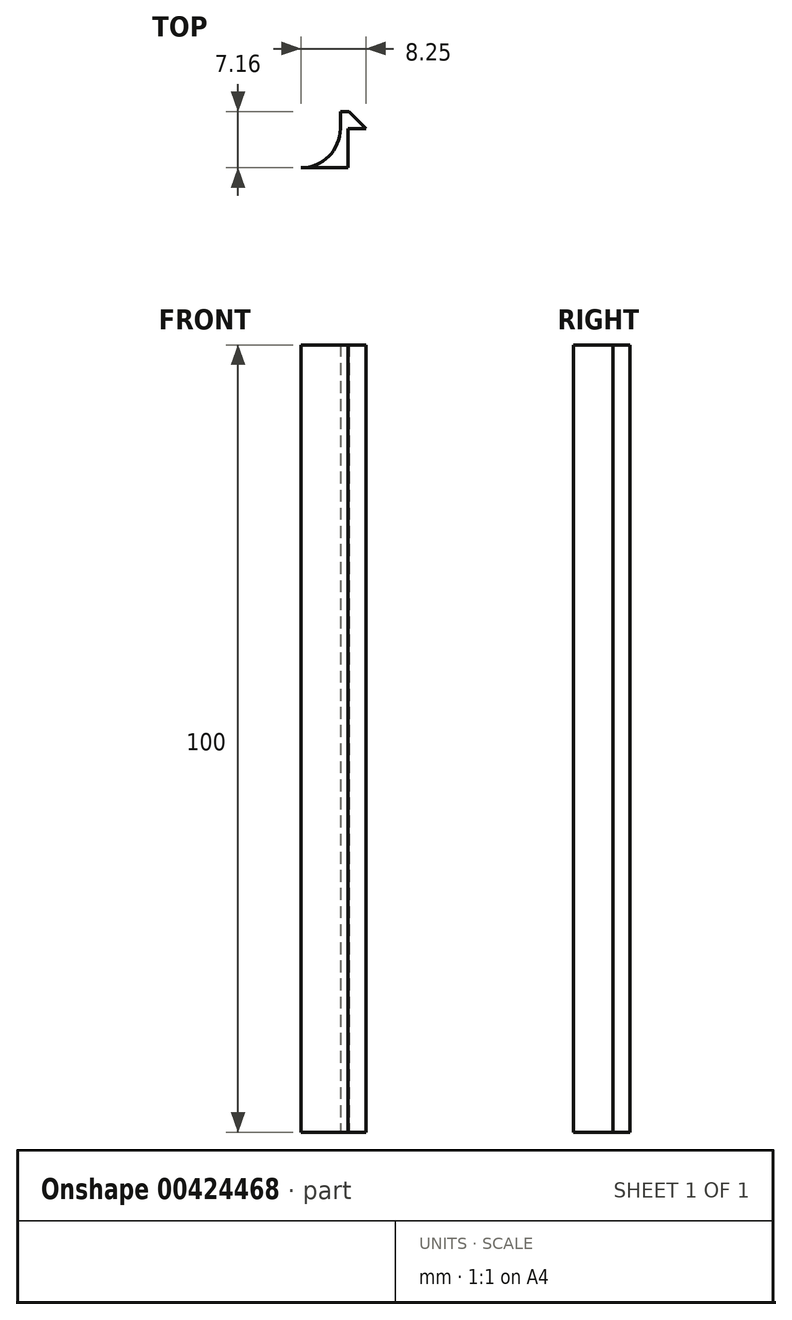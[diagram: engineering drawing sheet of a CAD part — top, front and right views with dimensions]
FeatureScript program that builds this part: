
annotation { "Feature Type Name" : "Feature", "Feature Type Description" : "" }
export const myFeature = defineFeature(function(context is Context, id is Id, definition is map)
    precondition{}
    {
        {
            var Q0;
            Q0=qCreatedBy(makeId("Top.planeOp"),FACE);
            var sketch = newSketch(context, id + "F0", { "sketchPlane" : qUnion([Q0])});
            skLineSegment(sketch, "E0", {"start": v(0, 0) * mm, "end": v(2.25, 0) * mm});
            skLineSegment(sketch, "E1", {"start": v(2.25, 0) * mm, "end": v(0.09, 2.16) * mm});
            skLineSegment(sketch, "E2", {"start": v(0, 0) * mm, "end": v(0, -5) * mm});
            skArc(sketch, "E3", {"start": v(-6, -5) * mm, "mid": v(-2.46, -3.54) * mm, "end": v(-1, 0) * mm});
            skLineSegment(sketch, "E4", {"start": v(-1, 0) * mm, "end": v(-1, 2.16) * mm});
            skLineSegment(sketch, "E5", {"start": v(0.09, 2.16) * mm, "end": v(-1, 2.16) * mm});
            skLineSegment(sketch, "E6", {"start": v(-6, -5) * mm, "end": v(-18.9, -2.72) * mm, "construction": true});
            skLineSegment(sketch, "E7", {"start": v(-18.9, -2.72) * mm, "end": v(-18.9, -5) * mm, "construction": true});
            skLineSegment(sketch, "E8", {"start": v(-6, -5) * mm, "end": v(0, -5) * mm});
            skLineSegment(sketch, "E9", {"start": v(-6, -5) * mm, "end": v(-18.9, -5) * mm, "construction": true});
            skSolve(sketch);
        }
        {
            var Q0;
            Q0=makeQuery(id+"F0.imprint","IMPRINT",FACE,{"disambiguationData":[TD([[makeQuery(id+"F0.imprint","IMPRINT",EDGE,{"derivedFrom":sQuery(id+"F0.wireOp",EDGE,"E0")}),1.0]])]});
            extrude(context, id + "F1", {"entities" : qUnion([Q0]), "depth" : 100 * mm});
        }
    });
